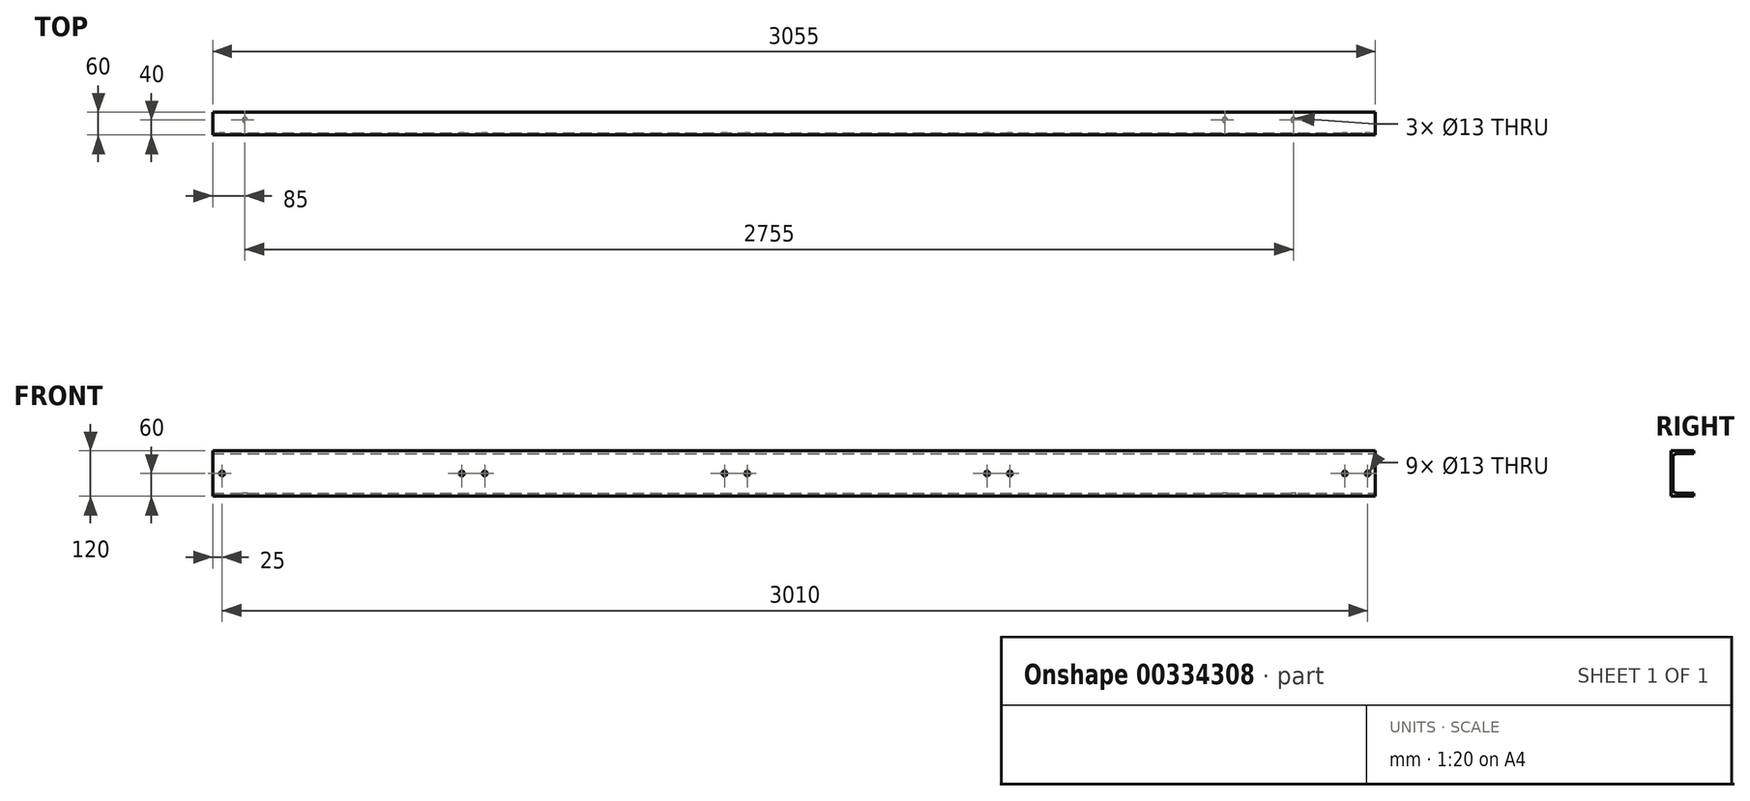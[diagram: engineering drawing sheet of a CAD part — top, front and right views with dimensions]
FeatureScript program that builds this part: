
annotation { "Feature Type Name" : "Feature", "Feature Type Description" : "" }
export const myFeature = defineFeature(function(context is Context, id is Id, definition is map)
    precondition{}
    {
        {
            assignVariable(context, id + "F0", {"name" : "L_Pro", "anyValue" : 2755 + 300});
        }
        {
            assignVariable(context, id + "F1", {"name" : "L_Hoe", "anyValue" : 120});
        }
        {
            var Q0;
            Q0=qCreatedBy(makeId("Right.planeOp"),FACE);
            var sketch = newSketch(context, id + "F2", { "sketchPlane" : qUnion([Q0])});
            skLineSegment(sketch, "E0", {"start": v(0, 0) * mm, "end": v(-60, 0) * mm});
            skLineSegment(sketch, "E1", {"start": v(-60, 0) * mm, "end": v(-60, 120) * mm});
            skLineSegment(sketch, "E2", {"start": v(-60, 120) * mm, "end": v(0, 120) * mm});
            skLineSegment(sketch, "E3", {"start": v(0, 120) * mm, "end": v(0, 112) * mm});
            skLineSegment(sketch, "E4", {"start": v(0, 112) * mm, "end": v(-43, 112) * mm});
            skLineSegment(sketch, "E5", {"start": v(-55, 100) * mm, "end": v(-55, 20) * mm});
            skLineSegment(sketch, "E6", {"start": v(-43, 8) * mm, "end": v(0, 8) * mm});
            skLineSegment(sketch, "E7", {"start": v(0, 8) * mm, "end": v(0, 0) * mm});
            skPoint(sketch, "E8.visualSharp", {"position": v(-55, 112) * mm});
            skArc(sketch, "E8.filletArc", {"start": v(-43, 112) * mm, "mid": v(-51.49, 108.49) * mm, "end": v(-55, 100) * mm});
            skPoint(sketch, "E9.visualSharp", {"position": v(-55, 8) * mm});
            skArc(sketch, "E9.filletArc", {"start": v(-55, 20) * mm, "mid": v(-51.49, 11.51) * mm, "end": v(-43, 8) * mm});
            skSolve(sketch);
        }
        {
            var Q0;
            Q0=qSketchRegion(id+"F2",true);
            var Q1;
            Q1=qConstructionFilter(qBodyType(qCreatedBy(id+"F2",EDGE),BodyType.WIRE),ConstructionObject.NO);
            extrude(context, id + "F3", {"entities" : qUnion([Q0]), "surfaceEntities" : qUnion([Q1]), "oppositeDirection" : true, "depth" : (getVariable(context, 'L_Pro')) * mm});
        }
        {
            var Q0;
            Q0=makeQuery(id+"F3.opExtrude","SWEPT_FACE",FACE,{"disambiguationData":[OSD([sQuery(id+"F2.wireOp",EDGE,"E6")])]});
            var sketch = newSketch(context, id + "F4", { "sketchPlane" : qUnion([Q0])});
            skCircle(sketch, "E10", {"center": v(-215, -20) * mm, "radius": 6.5 * mm});
            skCircle(sketch, "E11", {"center": v(-395, -20) * mm, "radius": 6.5 * mm});
            skCircle(sketch, "E12", {"center": v(-2970, -20) * mm, "radius": 6.5 * mm});
            skCircle(sketch, "E13", {"center": v(-2790, -20) * mm, "radius": 6.5 * mm, "construction": true});
            skSolve(sketch);
        }
        {
            var Q0;
            Q0=makeQuery(id+"F4.imprint","IMPRINT",FACE,{"disambiguationData":[TD([[makeQuery(id+"F4.imprint","IMPRINT",EDGE,{"derivedFrom":sQuery(id+"F4.wireOp",EDGE,"E10")}),1.0]])]});
            var Q1;
            Q1=makeQuery(id+"F4.imprint","IMPRINT",FACE,{"disambiguationData":[TD([[makeQuery(id+"F4.imprint","IMPRINT",EDGE,{"derivedFrom":sQuery(id+"F4.wireOp",EDGE,"E11")}),1.0]])]});
            var Q2;
            Q2=makeQuery(id+"F4.imprint","IMPRINT",FACE,{"disambiguationData":[TD([[makeQuery(id+"F4.imprint","IMPRINT",EDGE,{"derivedFrom":sQuery(id+"F4.wireOp",EDGE,"E12")}),1.0]])]});
            extrude(context, id + "F5", {"entities" : qUnion([Q0, Q1, Q2]), "operationType" : NewBodyOperationType.REMOVE, "endBound" : BoundingType.UP_TO_NEXT, "oppositeDirection" : true, "depth" : (2 * getVariable(context, 'L_Hoe')) * mm});
        }
        {
            var Q0;
            Q0=makeQuery(id+"F3.opExtrude","SWEPT_FACE",FACE,{"disambiguationData":[OSD([sQuery(id+"F2.wireOp",EDGE,"E1")])]});
            var sketch = newSketch(context, id + "F6", { "sketchPlane" : qUnion([Q0])});
            skCircle(sketch, "E14", {"center": v(-20, 60) * mm, "radius": 6.5 * mm});
            skPoint(sketch, "E14.centerSnap0", {"position": v(0, 60) * mm});
            skCircle(sketch, "E15", {"center": v(-80, 60) * mm, "radius": 6.5 * mm});
            skCircle(sketch, "E16", {"center": v(-960, 60) * mm, "radius": 6.5 * mm});
            skCircle(sketch, "E17", {"center": v(-1020, 60) * mm, "radius": 6.5 * mm});
            skCircle(sketch, "E18", {"center": v(-1650, 60) * mm, "radius": 6.5 * mm});
            skCircle(sketch, "E19", {"center": v(-1710, 60) * mm, "radius": 6.5 * mm});
            skCircle(sketch, "E20", {"center": v(-2340, 60) * mm, "radius": 6.5 * mm});
            skCircle(sketch, "E21", {"center": v(-2400, 60) * mm, "radius": 6.5 * mm});
            skCircle(sketch, "E22", {"center": v(-3030, 60) * mm, "radius": 6.5 * mm});
            skSolve(sketch);
        }
        {
            var Q0;
            Q0=qSketchRegion(id+"F6",true);
            extrude(context, id + "F7", {"entities" : qUnion([Q0]), "operationType" : NewBodyOperationType.REMOVE, "endBound" : BoundingType.THROUGH_ALL, "oppositeDirection" : true, "depth" : 25 * mm});
        }
    });
